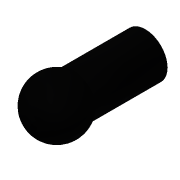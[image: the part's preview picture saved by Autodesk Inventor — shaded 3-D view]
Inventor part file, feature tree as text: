
AUTODESK INVENTOR PART (.ipt)
format: ipt  version: 2016 (Build 200138000, 138)  size: 118,272 bytes
history: native  units: in
note: dims shown in document units (in); Inventor stores cm internally (conversion verified against a paired STEP export)
features: sketch x3, extrude x2, revolve x1, fillet x1
ambient origin geometry x8: Origin, YZ Plane, XZ Plane, XY Plane, X Axis, Y Axis, Z Axis, Center Point
bodies: Solid1 (feature_tree)
feature tree (7):
  revolve  "Revolution1"  Angle=180.0deg
  extrude  "Extrusion1"  Depth=0.1181in
  extrude  "Extrusion2"  Depth=0.0591in
  fillet  "Fillet1"  Radius=0.315in
  sketch  "Sketch1"  dims[d0=0.1969in d1=180.0deg]
  sketch  "Sketch2"  dims[d2=0.1575in d3=0.1181in]
  sketch  "Sketch3"  dims[d4=0.315in d5=0.0in d6=0.1181in d7=0.315in d8=0.0in d9=0.0591in]
